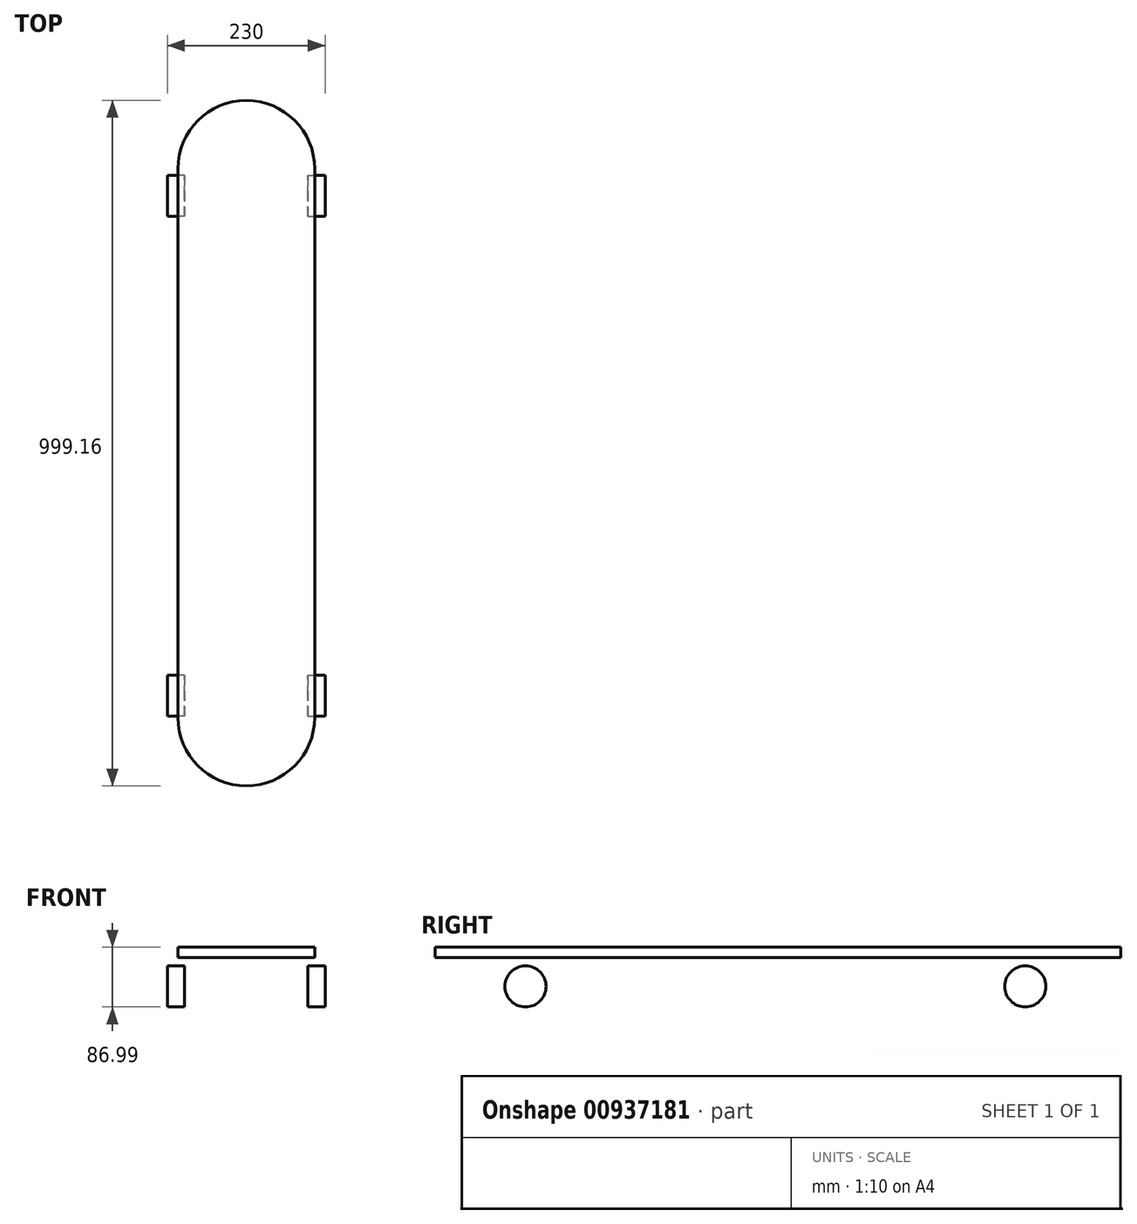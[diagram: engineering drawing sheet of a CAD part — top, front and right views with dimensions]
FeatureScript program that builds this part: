
annotation { "Feature Type Name" : "Feature", "Feature Type Description" : "" }
export const myFeature = defineFeature(function(context is Context, id is Id, definition is map)
    precondition{}
    {
        {
            var Q0;
            Q0=qCreatedBy(makeId("Top.planeOp"),FACE);
            var sketch = newSketch(context, id + "F0", { "sketchPlane" : qUnion([Q0])});
            skCircle(sketch, "E0", {"center": v(0, 0) * mm, "radius": 99.58 * mm});
            skLineSegment(sketch, "E1", {"start": v(0, 0) * mm, "end": v(0, -800) * mm, "construction": true});
            skCircle(sketch, "E2", {"center": v(0, -800) * mm, "radius": 99.58 * mm});
            skLineSegment(sketch, "E3", {"start": v(-99.58, -800) * mm, "end": v(-99.58, 0) * mm});
            skLineSegment(sketch, "E4", {"start": v(99.58, -800) * mm, "end": v(99.58, 0) * mm});
            skSolve(sketch);
        }
        {
            var Q0;
            Q0 = qSketchRegion(id + "F0", true);
            extrude(context, id + "F1", {"entities" : qUnion([Q0]), "depth" : 15 * mm, "offsetDistance" : 25 * mm});
        }
        {
            var Q0;
            Q0=qCreatedBy(makeId("Right.planeOp"),FACE);
            cPlane(context, id + "F2", {"entities" : qUnion([Q0]), "cplaneType" : CPlaneType.OFFSET, "offset" : 115 * mm, "oppositeDirection" : true, "width" : 150 * mm, "height" : 150 * mm});
        }
        {
            var Q0;
            Q0=qCreatedBy(id+"F2.planeOp",FACE);
            var sketch = newSketch(context, id + "F3", { "sketchPlane" : qUnion([Q0])});
            skCircle(sketch, "E5", {"center": v(-39.69, -41.99) * mm, "radius": 30 * mm});
            skCircle(sketch, "E6", {"center": v(-767.85, -41.99) * mm, "radius": 30 * mm});
            skSolve(sketch);
        }
        {
            var Q0;
            Q0 = qSketchRegion(id + "F3", true);
            extrude(context, id + "F4", {"entities" : qUnion([Q0]), "depth" : 25 * mm, "offsetDistance" : 25 * mm});
        }
        {
            var Q0;
            Q0=makeQuery(id+"F4.opExtrude","SWEPT_BODY",BODY,{"disambiguationData":[OSD([sQuery(id+"F3.wireOp",EDGE,"E5")])]});
            var Q1;
            Q1=makeQuery(id+"F4.opExtrude","SWEPT_BODY",BODY,{"disambiguationData":[OSD([sQuery(id+"F3.wireOp",EDGE,"E6")])]});
            var Q2;
            Q2=qCreatedBy(makeId("Right.planeOp"),FACE);
            mirror(context, id + "F5", {"entities" : qUnion([Q0, Q1]), "mirrorPlane" : qUnion([Q2])});
        }
    });
